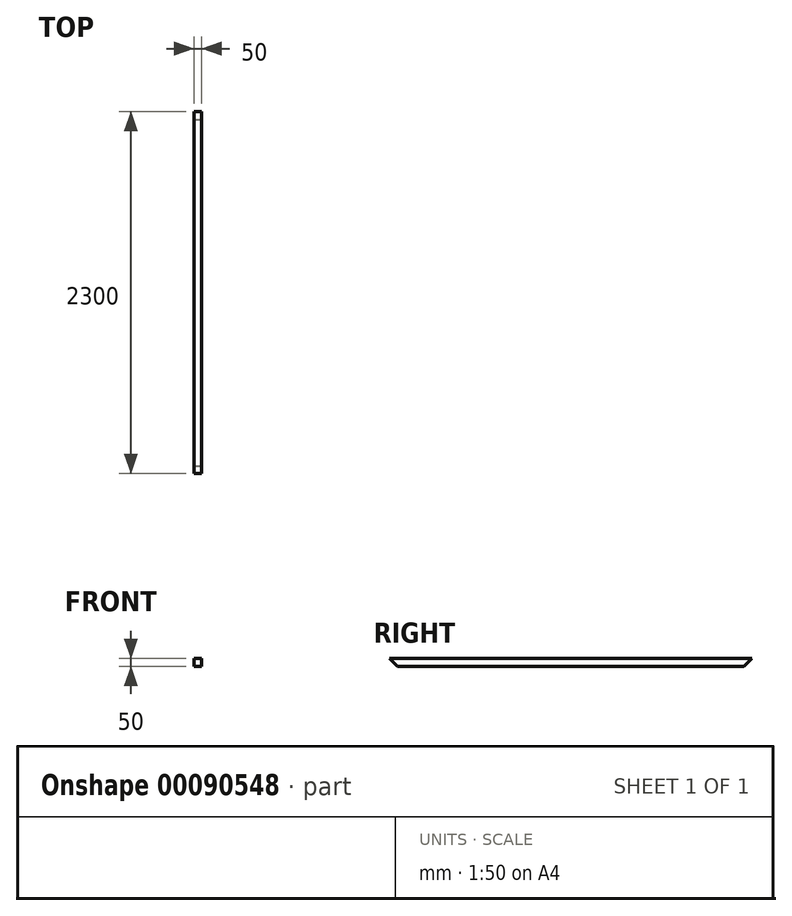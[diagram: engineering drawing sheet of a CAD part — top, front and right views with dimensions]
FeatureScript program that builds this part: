
annotation { "Feature Type Name" : "Feature", "Feature Type Description" : "" }
export const myFeature = defineFeature(function(context is Context, id is Id, definition is map)
    precondition{}
    {
        {
            var Q0;
            Q0=qCreatedBy(makeId("Front.planeOp"),FACE);
            var sketch = newSketch(context, id + "F0", { "sketchPlane" : qUnion([Q0])});
            skLineSegment(sketch, "E0.bottom", {"start": v(25, -25) * mm, "end": v(-25, -25) * mm});
            skLineSegment(sketch, "E0.top", {"start": v(25, 25) * mm, "end": v(-25, 25) * mm});
            skLineSegment(sketch, "E0.left", {"start": v(25, -25) * mm, "end": v(25, 25) * mm});
            skLineSegment(sketch, "E0.right", {"start": v(-25, -25) * mm, "end": v(-25, 25) * mm});
            skPoint(sketch, "E0.middle", {"position": v(0, 0) * mm});
            skSolve(sketch);
        }
        {
            var Q0;
            Q0=qSketchRegion(id+"F0",true);
            extrude(context, id + "F1", {"entities" : qUnion([Q0]), "depth" : 2300 * mm});
        }
        {
            var Q0;
            Q0=qCreatedBy(makeId("Right.planeOp"),FACE);
            var sketch = newSketch(context, id + "F2", { "sketchPlane" : qUnion([Q0])});
            skLineSegment(sketch, "E1", {"start": v(-2250, -25) * mm, "end": v(-2300, 25) * mm});
            skLineSegment(sketch, "E2", {"start": v(-50, -25) * mm, "end": v(0, 25) * mm});
            skLineSegment(sketch, "E3", {"start": v(-2300, -25) * mm, "end": v(-2250, -25) * mm});
            skLineSegment(sketch, "E4", {"start": v(-2300, 25) * mm, "end": v(-2300, -25) * mm});
            skLineSegment(sketch, "E5", {"start": v(0, 25) * mm, "end": v(0, -25) * mm});
            skLineSegment(sketch, "E6", {"start": v(-50, -25) * mm, "end": v(0, -25) * mm});
            skSolve(sketch);
        }
        {
            var Q0;
            Q0=qSketchRegion(id+"F2",true);
            extrude(context, id + "F3", {"entities" : qUnion([Q0]), "operationType" : NewBodyOperationType.REMOVE, "endBound" : BoundingType.THROUGH_ALL, "oppositeDirection" : true, "depth" : 25 * mm, "hasSecondDirection" : true, "secondDirectionBound" : SecondDirectionBoundingType.THROUGH_ALL, "secondDirectionOppositeDirection" : false, "secondDirectionDepth" : 25 * mm});
        }
    });
